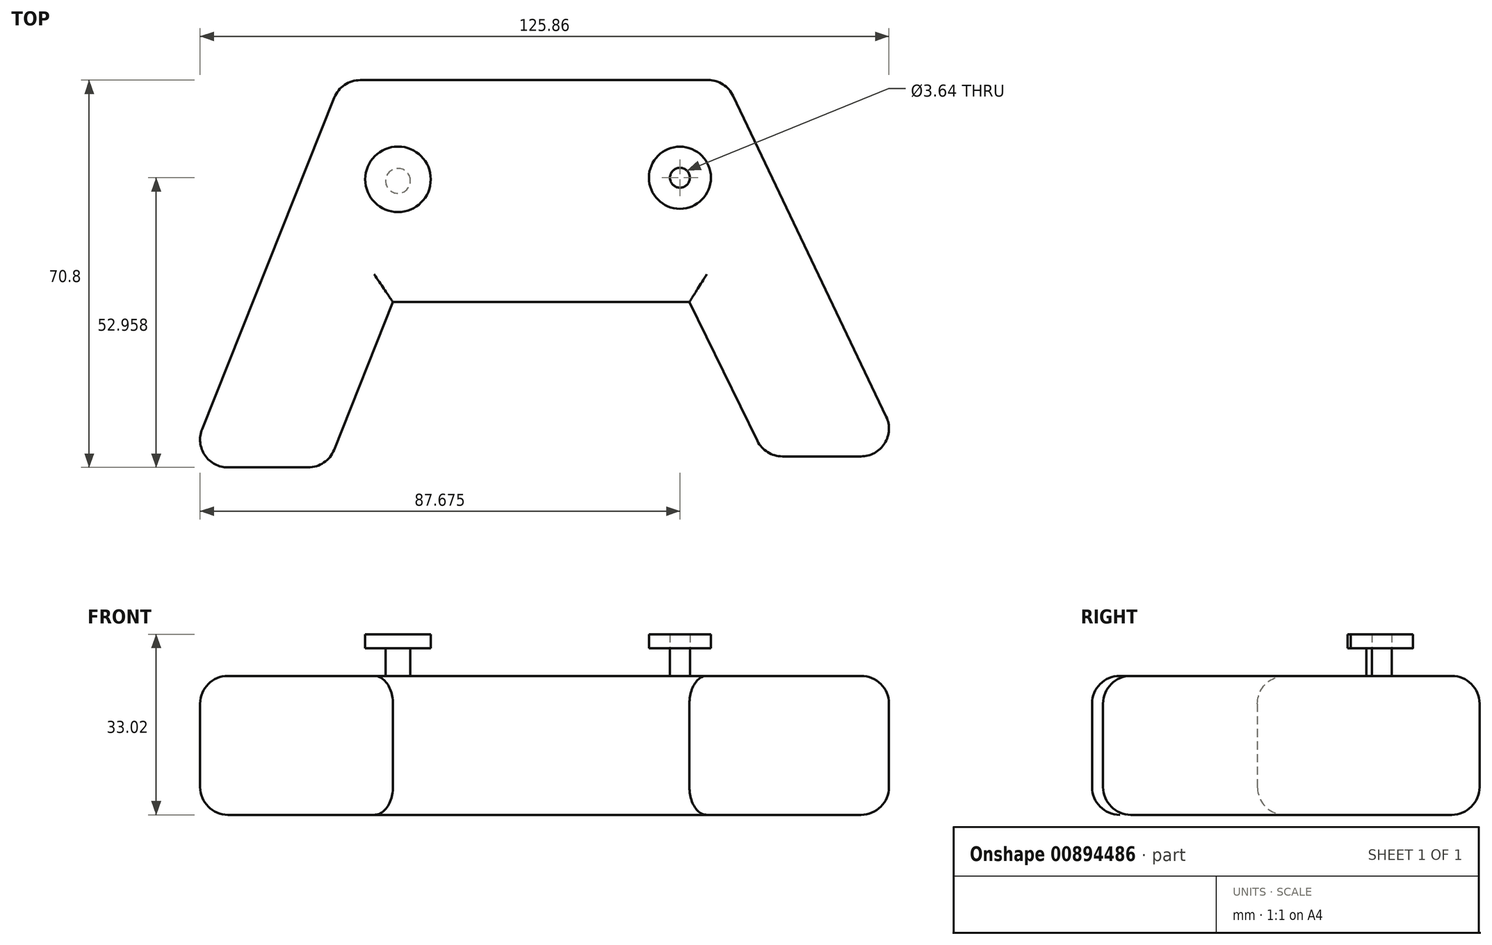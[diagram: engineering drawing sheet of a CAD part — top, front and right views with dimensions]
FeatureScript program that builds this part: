
annotation { "Feature Type Name" : "Feature", "Feature Type Description" : "" }
export const myFeature = defineFeature(function(context is Context, id is Id, definition is map)
    precondition{}
    {
        {
            var Q0;
            Q0=qCreatedBy(makeId("Top.planeOp"),FACE);
            var sketch = newSketch(context, id + "F0", { "sketchPlane" : qUnion([Q0])});
            skLineSegment(sketch, "E0", {"start": v(-53.39, -46.77) * mm, "end": v(-25.18, 24.03) * mm});
            skLineSegment(sketch, "E1", {"start": v(-25.18, 24.03) * mm, "end": v(45.04, 24.03) * mm});
            skLineSegment(sketch, "E2", {"start": v(45.04, 24.03) * mm, "end": v(77.85, -44.75) * mm});
            skLineSegment(sketch, "E3", {"start": v(77.85, -44.75) * mm, "end": v(52.24, -44.75) * mm});
            skLineSegment(sketch, "E4", {"start": v(52.24, -44.75) * mm, "end": v(38.42, -16.55) * mm});
            skLineSegment(sketch, "E5", {"start": v(-53.39, -46.77) * mm, "end": v(-27.77, -46.77) * mm});
            skLineSegment(sketch, "E6", {"start": v(-27.77, -46.77) * mm, "end": v(-15.73, -16.55) * mm});
            skLineSegment(sketch, "E7", {"start": v(-15.73, -16.55) * mm, "end": v(38.42, -16.55) * mm});
            skLineSegment(sketch, "E8", {"start": v(52.24, -46.77) * mm, "end": v(79.3, -46.77) * mm});
            skLineSegment(sketch, "E9", {"start": v(79.3, -46.77) * mm, "end": v(75.47, -39.75) * mm});
            skLineSegment(sketch, "E10", {"start": v(52.24, -44.75) * mm, "end": v(52.24, -46.77) * mm});
            skSolve(sketch);
        }
        {
            var Q0;
            Q0=makeQuery(id+"F0.imprint","IMPRINT",FACE,{"disambiguationData":[TD([[makeQuery(id+"F0.imprint","IMPRINT",EDGE,{"derivedFrom":sQuery(id+"F0.wireOp",EDGE,"E0")}),-1.0]])]});
            extrude(context, id + "F1", {"entities" : qUnion([Q0]), "depth" : 25.4 * mm, "offsetDistance" : 25.4 * mm});
        }
        {
            var Q0;
            Q0=makeQuery(id+"F1.opExtrude","SWEPT_EDGE",EDGE,{"disambiguationData":[OSD([sQuery(id+"F0.wireOp",EDGE,"E0"),sQuery(id+"F0.wireOp",EDGE,"E1")])]});
            var Q1;
            Q1=makeQuery(id+"F1.opExtrude","SWEPT_EDGE",EDGE,{"disambiguationData":[OSD([sQuery(id+"F0.wireOp",EDGE,"E1"),sQuery(id+"F0.wireOp",EDGE,"E2")])]});
            var Q2;
            Q2=makeQuery(id+"F1.opExtrude","SWEPT_EDGE",EDGE,{"disambiguationData":[OSD([sQuery(id+"F0.wireOp",EDGE,"E0"),sQuery(id+"F0.wireOp",EDGE,"E5")])]});
            var Q3;
            Q3=makeQuery(id+"F1.opExtrude","SWEPT_EDGE",EDGE,{"disambiguationData":[OSD([sQuery(id+"F0.wireOp",EDGE,"E3"),sQuery(id+"F0.wireOp",EDGE,"E4"),sQuery(id+"F0.wireOp",EDGE,"E10")])]});
            var Q4;
            Q4=makeQuery(id+"F1.opExtrude","SWEPT_EDGE",EDGE,{"disambiguationData":[OSD([sQuery(id+"F0.wireOp",EDGE,"E2"),sQuery(id+"F0.wireOp",EDGE,"E3")])]});
            var Q5;
            Q5=makeQuery(id+"F1.opExtrude","SWEPT_EDGE",EDGE,{"disambiguationData":[OSD([sQuery(id+"F0.wireOp",EDGE,"E5"),sQuery(id+"F0.wireOp",EDGE,"E6")])]});
            fillet(context, id + "F2", {"entities" : qUnion([Q0, Q1, Q2, Q3, Q4, Q5]), "radius" : 5.08 * mm, "tangentPropagation" : true, "allowEdgeOverflow" : false});
        }
        {
            var Q0;
            Q0=makeQuery(id+"F1.opExtrude","CAP_EDGE",EDGE,{"disambiguationData":[OSD([sQuery(id+"F0.wireOp",EDGE,"E5")])],"isStart":false});
            var Q1;
            Q1=makeQuery(id+"F1.opExtrude","CAP_EDGE",EDGE,{"disambiguationData":[OSD([sQuery(id+"F0.wireOp",EDGE,"E6")])],"isStart":false});
            var Q2;
            Q2=makeQuery(id+"F1.opExtrude","CAP_EDGE",EDGE,{"disambiguationData":[OSD([sQuery(id+"F0.wireOp",EDGE,"E7")])],"isStart":false});
            var Q3;
            Q3=makeQuery(id+"F1.opExtrude","CAP_EDGE",EDGE,{"disambiguationData":[OSD([sQuery(id+"F0.wireOp",EDGE,"E4")])],"isStart":false});
            var Q4;
            Q4=makeQuery(id+"F1.opExtrude","CAP_EDGE",EDGE,{"disambiguationData":[OSD([sQuery(id+"F0.wireOp",EDGE,"E3")])],"isStart":false});
            var Q5;
            Q5=makeQuery(id+"F1.opExtrude","CAP_EDGE",EDGE,{"disambiguationData":[OSD([sQuery(id+"F0.wireOp",EDGE,"E2")])],"isStart":false});
            var Q6;
            Q6=makeQuery(id+"F1.opExtrude","CAP_EDGE",EDGE,{"disambiguationData":[OSD([sQuery(id+"F0.wireOp",EDGE,"E0")])],"isStart":false});
            var Q7;
            Q7=makeQuery(id+"F1.opExtrude","CAP_EDGE",EDGE,{"disambiguationData":[OSD([sQuery(id+"F0.wireOp",EDGE,"E1")])],"isStart":false});
            var Q8;
            Q8=makeQuery(id+"F1.opExtrude","CAP_EDGE",EDGE,{"disambiguationData":[OSD([sQuery(id+"F0.wireOp",EDGE,"E5")])],"isStart":true});
            var Q9;
            Q9=makeQuery(id+"F1.opExtrude","CAP_EDGE",EDGE,{"disambiguationData":[OSD([sQuery(id+"F0.wireOp",EDGE,"E7")])],"isStart":true});
            var Q10;
            Q10=makeQuery(id+"F1.opExtrude","CAP_EDGE",EDGE,{"disambiguationData":[OSD([sQuery(id+"F0.wireOp",EDGE,"E6")])],"isStart":true});
            var Q11;
            Q11=makeQuery(id+"F1.opExtrude","CAP_EDGE",EDGE,{"disambiguationData":[OSD([sQuery(id+"F0.wireOp",EDGE,"E3")])],"isStart":true});
            var Q12;
            Q12=makeQuery(id+"F1.opExtrude","CAP_EDGE",EDGE,{"disambiguationData":[OSD([sQuery(id+"F0.wireOp",EDGE,"E2")])],"isStart":true});
            var Q13;
            Q13=makeQuery(id+"F1.opExtrude","CAP_EDGE",EDGE,{"disambiguationData":[OSD([sQuery(id+"F0.wireOp",EDGE,"E1")])],"isStart":true});
            var Q14;
            Q14=makeQuery(id+"F1.opExtrude","CAP_EDGE",EDGE,{"disambiguationData":[OSD([sQuery(id+"F0.wireOp",EDGE,"E0")])],"isStart":true});
            fillet(context, id + "F3", {"entities" : qUnion([Q0, Q1, Q2, Q3, Q4, Q5, Q6, Q7, Q8, Q9, Q10, Q11, Q12, Q13, Q14]), "radius" : 5.08 * mm, "tangentPropagation" : true, "allowEdgeOverflow" : false});
        }
        {
            var Q0;
            Q0=makeQuery(id+"F1.opExtrude","CAP_FACE",FACE,{"disambiguationData":[OSD([sQuery(id+"F0.wireOp",EDGE,"E0"),sQuery(id+"F0.wireOp",EDGE,"E1"),sQuery(id+"F0.wireOp",EDGE,"E2"),sQuery(id+"F0.wireOp",EDGE,"E3"),sQuery(id+"F0.wireOp",EDGE,"E5"),sQuery(id+"F0.wireOp",EDGE,"E4"),sQuery(id+"F0.wireOp",EDGE,"E6"),sQuery(id+"F0.wireOp",EDGE,"E7")])],"isStart":false});
            var sketch = newSketch(context, id + "F4", { "sketchPlane" : qUnion([Q0])});
            skCircle(sketch, "E11", {"center": v(36.7, 6.19) * mm, "radius": 1.82 * mm});
            skCircle(sketch, "E12", {"center": v(-14.82, 5.61) * mm, "radius": 2.27 * mm});
            skSolve(sketch);
        }
        {
            var Q0;
            Q0=makeQuery(id+"F4.imprint","IMPRINT",FACE,{"disambiguationData":[TD([[makeQuery(id+"F4.imprint","IMPRINT",EDGE,{"derivedFrom":sQuery(id+"F4.wireOp",EDGE,"E12")}),1.0]])]});
            var Q1;
            Q1=makeQuery(id+"F4.imprint","IMPRINT",FACE,{"disambiguationData":[TD([[makeQuery(id+"F4.imprint","IMPRINT",EDGE,{"derivedFrom":sQuery(id+"F4.wireOp",EDGE,"E11")}),1.0]])]});
            extrude(context, id + "F5", {"entities" : qUnion([Q0, Q1]), "operationType" : NewBodyOperationType.ADD, "depth" : 5.08 * mm, "offsetDistance" : 25.4 * mm});
        }
        {
            var Q0;
            Q0=makeQuery(id+"F5.opExtrude","CAP_FACE",FACE,{"disambiguationData":[OSD([sQuery(id+"F4.wireOp",EDGE,"E11")])],"isStart":false});
            var sketch = newSketch(context, id + "F6", { "sketchPlane" : qUnion([Q0])});
            skCircle(sketch, "E13", {"center": v(-14.82, 5.9) * mm, "radius": 5.99 * mm});
            skCircle(sketch, "E14", {"center": v(36.7, 6.19) * mm, "radius": 5.67 * mm});
            skSolve(sketch);
        }
        {
            var Q0;
            Q0=makeQuery(id+"F6.imprint","IMPRINT",FACE,{"disambiguationData":[TD([[makeQuery(id+"F6.imprint","IMPRINT",EDGE,{"derivedFrom":sQuery(id+"F6.wireOp",EDGE,"E13")}),1.0]])]});
            var Q1;
            Q1=makeQuery(id+"F6.imprint","IMPRINT",FACE,{"disambiguationData":[TD([[makeQuery(id+"F6.imprint","IMPRINT",EDGE,{"derivedFrom":sQuery(id+"F6.wireOp",EDGE,"E14")}),1.0]])]});
            extrude(context, id + "F7", {"entities" : qUnion([Q0, Q1]), "operationType" : NewBodyOperationType.ADD, "depth" : 2.54 * mm, "offsetDistance" : 25.4 * mm});
        }
        {
            var Q0;
            Q0=makeQuery(id+"F5.opExtrude","CAP_FACE",FACE,{"disambiguationData":[OSD([sQuery(id+"F4.wireOp",EDGE,"E11")])],"isStart":false});
            extrude(context, id + "F8", {"entities" : qUnion([Q0]), "depth" : 2.54 * mm, "offsetDistance" : 25.4 * mm});
        }
    });
